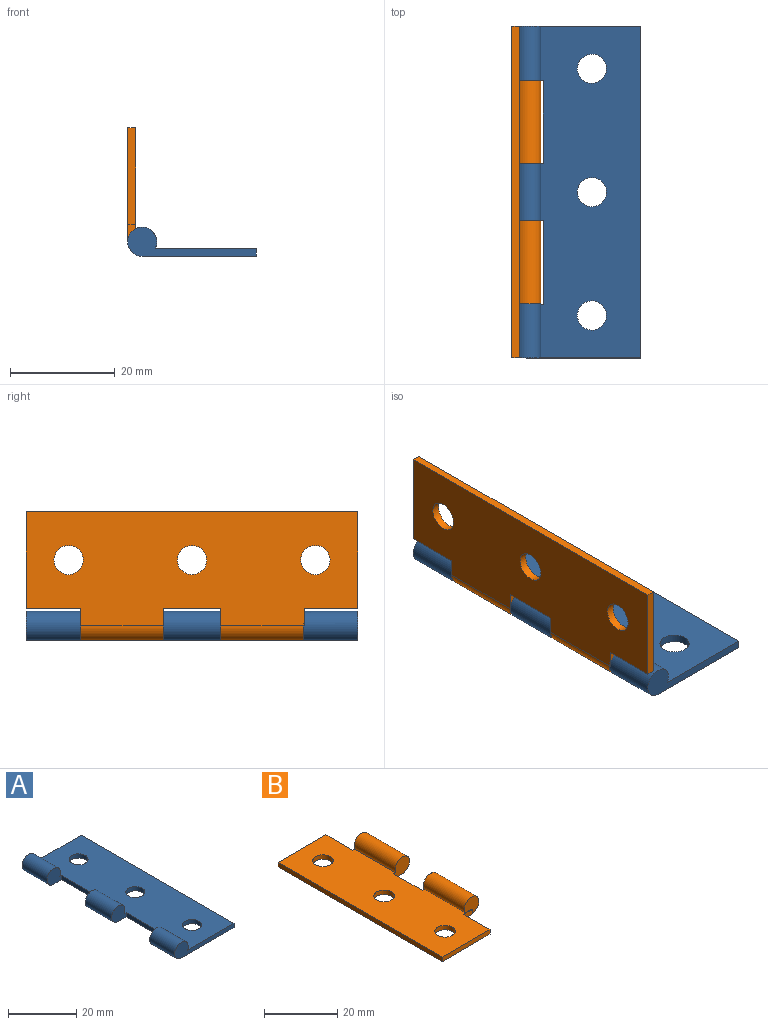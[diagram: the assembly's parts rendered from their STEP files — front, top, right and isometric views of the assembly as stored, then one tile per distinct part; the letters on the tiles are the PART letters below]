
ASSEMBLY  parts=2 mates=1
PART A: 18 faces, bbox 24.6x63.5x5.6 mm
  f0: plane 63.5x19.36mm, normal (0,0,1), area 1129.5mm2, adj f1,f2,f3,f4,f5,f6,f7,f8
  f1: plane 24.64x5.59mm, normal (0,-1,0), area 55.1mm2, adj f0,f2,f13,f15
  f2: plane 63.5x1.52mm, normal (1,0,0), area 96.8mm2, adj f0,f1,f3,f13
  f3: plane 24.64x5.59mm, normal (0,1,0), area 55.1mm2, adj f0,f2,f13,f17
  f4: plane 6.1x5.59mm, normal (0,-1,0), area 26.8mm2, adj f0,f5,f13,f17
  f5: plane 15.88x1.52mm, normal (-1,0,0), area 24.2mm2, adj f0,f4,f6,f13
  f6: plane 6.1x5.59mm, normal (0,1,0), area 26.8mm2, adj f0,f5,f13,f14
  f7: plane 6.1x5.59mm, normal (0,-1,0), area 26.8mm2, adj f0,f8,f13,f14
  f8: plane 16.13x1.52mm, normal (-1,0,0), area 24.6mm2, adj f0,f7,f9,f13
  f9: plane 3.3x1.52mm, normal (0,1,0), area 2.3mm2, adj f0,f8,f13,f15
  f10: cylinder r=2.79mm len=5.59mm, axis (0,0,-1), area 26.8mm2, adj f0,f13
  f11: cylinder r=2.79mm len=5.59mm, axis (0,0,-1), area 26.8mm2, adj f0,f13
  f12: cylinder r=2.79mm len=5.59mm, axis (0,0,-1), area 26.8mm2, adj f0,f13
  f13: plane 63.5x21.84mm, normal (0,0,-1), area 1207.8mm2, adj f1,f2,f3,f4,f5,f6,f7,f8
  f14: cylinder r=2.79mm len=10.92mm, axis (0,-1,0), area 158.2mm2, adj f0,f6,f7,f13
  f15: cylinder r=2.79mm len=10.41mm, axis (0,-1,0), area 151.6mm2, adj f0,f1,f9,f13,f16
  f16: plane 5.59x5.59mm, normal (0,1,0), area 24.5mm2, adj f15
  f17: cylinder r=2.79mm len=10.41mm, axis (0,1,0), area 150.8mm2, adj f0,f3,f4,f13
PART B: 19 faces, bbox 24.6x63.5x5.6 mm
  f0: plane 63.5x21.84mm, normal (0,0,1), area 1130.5mm2, adj f1,f2,f3,f4,f5,f6,f7,f8
  f1: plane 10.16x1.52mm, normal (1,0,0), area 15.5mm2, adj f0,f2,f14,f15
  f2: plane 3.3x1.52mm, normal (0,-1,0), area 5mm2, adj f0,f1,f3,f15
  f3: plane 1.52x0.25mm, normal (1,0,0), area 0.4mm2, adj f0,f2,f15,f16
  f4: plane 6.1x5.59mm, normal (0,1,0), area 26.8mm2, adj f0,f5,f15,f17
  f5: plane 10.92x1.52mm, normal (1,0,0), area 16.6mm2, adj f0,f4,f6,f15
  f6: plane 6.1x5.59mm, normal (0,-1,0), area 26.8mm2, adj f0,f5,f15,f18
  f7: plane 6.1x5.59mm, normal (0,1,0), area 26.8mm2, adj f0,f8,f15,f18
  f8: plane 10.41x1.52mm, normal (1,0,0), area 15.9mm2, adj f0,f7,f9,f15
  f9: plane 18.54x1.52mm, normal (0,1,0), area 28.3mm2, adj f0,f8,f10,f15
  f10: plane 63.5x1.52mm, normal (-1,0,0), area 96.8mm2, adj f0,f9,f14,f15
  f11: cylinder r=2.79mm len=5.59mm, axis (0,0,-1), area 26.8mm2, adj f0,f15
  f12: cylinder r=2.79mm len=5.59mm, axis (0,0,-1), area 26.8mm2, adj f0,f15
  f13: cylinder r=2.79mm len=5.59mm, axis (0,0,-1), area 26.8mm2, adj f0,f15
  f14: plane 18.54x1.52mm, normal (0,-1,0), area 28.3mm2, adj f0,f1,f10,f15
  f15: plane 63.5x21.84mm, normal (0,0,-1), area 1209.5mm2, adj f1,f2,f3,f4,f5,f6,f7,f8
  f16: plane 5.59x5.59mm, normal (0,-1,0), area 21.8mm2, adj f0,f3,f17
  f17: cylinder r=2.79mm len=15.88mm, axis (0,1,0), area 229.9mm2, adj f0,f4,f15,f16
  f18: cylinder r=2.79mm len=15.88mm, axis (0,-1,0), area 229.9mm2, adj f0,f6,f7,f15
PLACE A at identity
PLACE B rot(axis=(0,1,0),90deg) t=(-2.79,0,2.79)mm
MATE revolute A.f14 <-> B.f17  axis (0,-1,0) through (0,21.34,2.79)mm
